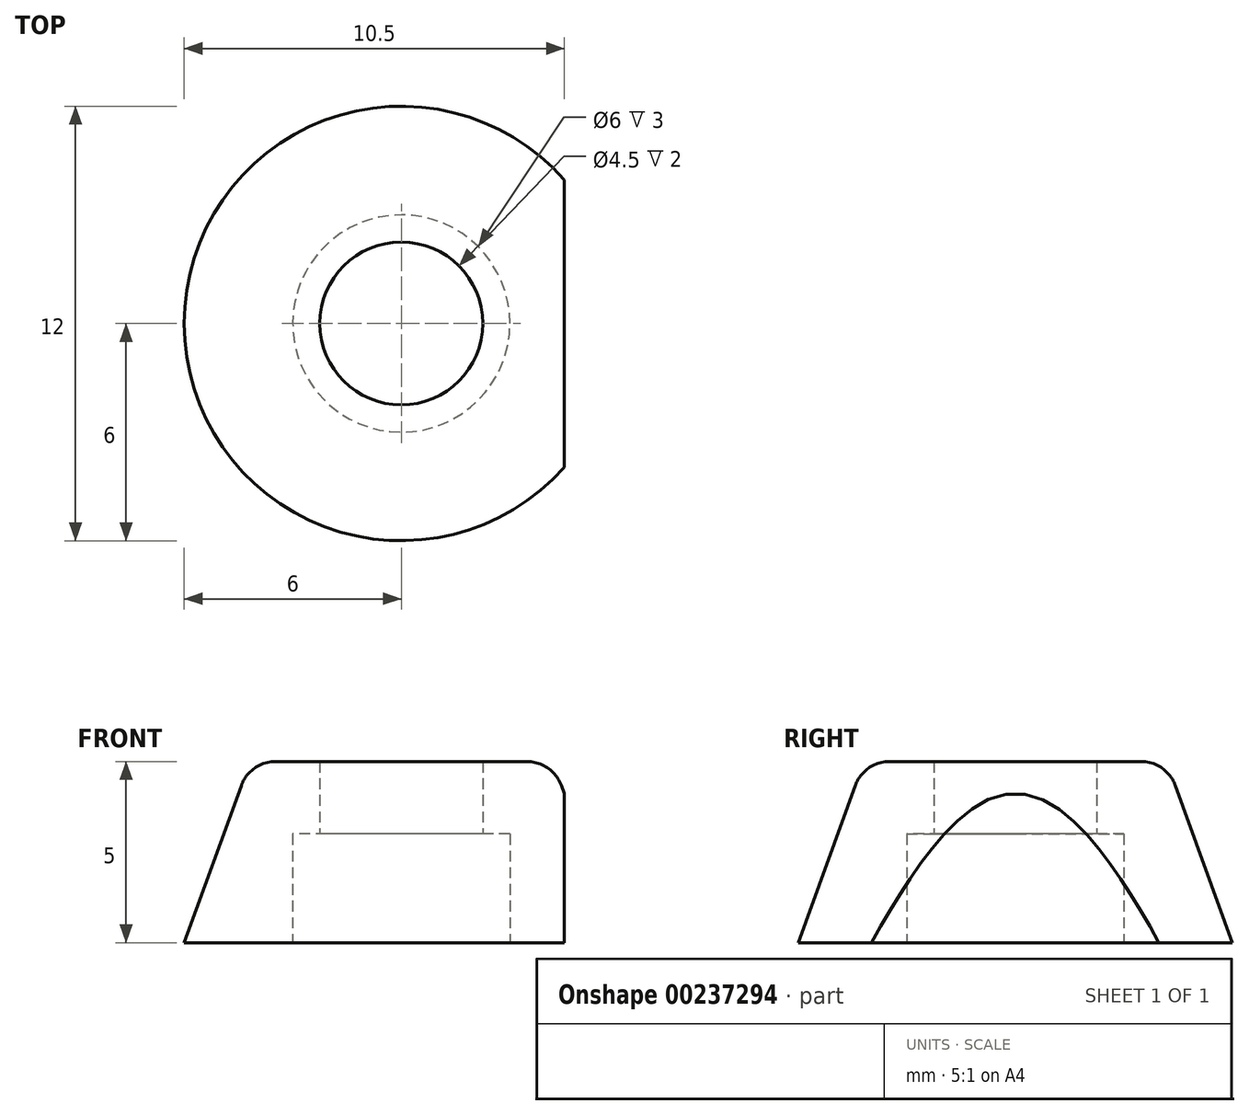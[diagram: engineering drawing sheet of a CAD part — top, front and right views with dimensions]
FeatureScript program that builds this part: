
annotation { "Feature Type Name" : "Feature", "Feature Type Description" : "" }
export const myFeature = defineFeature(function(context is Context, id is Id, definition is map)
    precondition{}
    {
        {
            var Q0;
            Q0=qCreatedBy(makeId("Top.planeOp"),FACE);
            var sketch = newSketch(context, id + "F0", { "sketchPlane" : qUnion([Q0])});
            skCircle(sketch, "E0", {"center": v(0, 0) * mm, "radius": 2.25 * mm});
            skCircle(sketch, "E1", {"center": v(0, 0) * mm, "radius": 3 * mm});
            skCircle(sketch, "E2", {"center": v(0, 0) * mm, "radius": 6 * mm});
            skLineSegment(sketch, "E3", {"start": v(4.5, 3.97) * mm, "end": v(4.5, -3.97) * mm});
            skSolve(sketch);
        }
        {
            var Q0;
            Q0=makeQuery(id+"F0.imprint","IMPRINT",FACE,{"disambiguationData":[TD([[makeQuery(id+"F0.imprint","IMPRINT",EDGE,{"derivedFrom":sQuery(id+"F0.wireOp",EDGE,"E1")}),-1.0]])]});
            var Q1;
            Q1=makeQuery(id+"F0.imprint","IMPRINT",FACE,{"disambiguationData":[TD([[makeQuery(id+"F0.imprint","IMPRINT",EDGE,{"derivedFrom":sQuery(id+"F0.wireOp",EDGE,"E0")}),1.0]])]});
            var Q2;
            Q2=makeQuery(id+"F0.imprint","IMPRINT",FACE,{"disambiguationData":[TD([[makeQuery(id+"F0.imprint","IMPRINT",EDGE,{"derivedFrom":sQuery(id+"F0.wireOp",EDGE,"E0")}),-1.0]])]});
            var Q3;
            {var subQ0=sQuery(id+"F0.wireOp",EDGE,"E3");Q3=makeQuery(id+"F0.imprint","IMPRINT",FACE,{"disambiguationData":[TD([[makeQuery(id+"F0.imprint","IMPRINT",EDGE,{"derivedFrom":subQ0}),1.0]])]});}
            extrude(context, id + "F1", {"entities" : qUnion([Q0, Q1, Q2, Q3]), "depth" : 5 * mm, "offsetDistance" : 25 * mm, "hasDraft" : true, "draftAngle" : 20 * degree, "draftPullDirection" : true});
        }
        {
            var Q0;
            Q0=makeQuery(id+"F0.imprint","IMPRINT",FACE,{"disambiguationData":[TD([[makeQuery(id+"F0.imprint","IMPRINT",EDGE,{"derivedFrom":sQuery(id+"F0.wireOp",EDGE,"E0")}),-1.0]])]});
            extrude(context, id + "F2", {"entities" : qUnion([Q0]), "operationType" : NewBodyOperationType.REMOVE, "depth" : 3 * mm, "offsetDistance" : 25 * mm});
        }
        {
            var Q0;
            Q0=makeQuery(id+"F0.imprint","IMPRINT",FACE,{"disambiguationData":[TD([[makeQuery(id+"F0.imprint","IMPRINT",EDGE,{"derivedFrom":sQuery(id+"F0.wireOp",EDGE,"E0")}),1.0]])]});
            extrude(context, id + "F3", {"entities" : qUnion([Q0]), "operationType" : NewBodyOperationType.REMOVE, "depth" : 25 * mm, "offsetDistance" : 25 * mm});
        }
        {
            var Q0;
            Q0=makeQuery(id+"F1.opExtrude","CAP_EDGE",EDGE,{"disambiguationData":[OSD([sQuery(id+"F0.wireOp",EDGE,"E2")])],"isStart":false});
            fillet(context, id + "F4", {"entities" : qUnion([Q0]), "radius" : 1 * mm, "tangentPropagation" : true, "allowEdgeOverflow" : false});
        }
        {
            var Q0;
            {var subQ0=sQuery(id+"F0.wireOp",EDGE,"E3");Q0=makeQuery(id+"F0.imprint","IMPRINT",FACE,{"disambiguationData":[TD([[makeQuery(id+"F0.imprint","IMPRINT",EDGE,{"derivedFrom":subQ0}),1.0]])]});}
            extrude(context, id + "F5", {"entities" : qUnion([Q0]), "operationType" : NewBodyOperationType.REMOVE, "depth" : 25 * mm, "offsetDistance" : 25 * mm});
        }
    });
